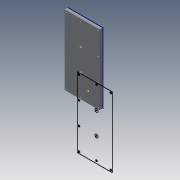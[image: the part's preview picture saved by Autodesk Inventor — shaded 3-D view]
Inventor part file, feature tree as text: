
AUTODESK INVENTOR PART (.ipt)
format: ipt  version: 2015 (Build 190159000, 159)  size: 136,192 bytes
history: native  units: mm
features: other x5, sketch x2, extrude x1, projected_geometry x1
ambient origin geometry x8: Origin, YZ Plane, XZ Plane, XY Plane, X Axis, Y Axis, Z Axis, Center Point
bodies: Body1 (feature_tree)
feature tree (9):
  other  "Blocks"
  extrude  "Extrusion5"  Depth=10.0mm
  sketch  "Sketch2"  dims[d9=70.0mm d13=35.0mm d14=50.0mm d17=75.0mm d18=185.0mm d19=35.0mm d22=5.0mm d23=5.0mm d24=5.0mm d25=5.0mm d26=5.0mm d27=5.0mm d28=5.0mm d29=5.0mm d30=5.0mm d31=5.0mm d32=5.0mm d33=75.0mm d34=5.0mm d35=75.0mm d36=5.0mm d37=5.0mm d38=5.0mm d39=5.0mm d42=5.0mm d43=50.0mm d46=5.0mm d47=5.0mm d48=50.0mm d49=10.0mm d50=0.0mm]
  other  "DXF"
  sketch  "Sketch1"  dims[d2=200.0mm d5=10.0mm]
  projected_geometry  "Projected Loop1"
  other  "Block1"
  other  "Block1:1"
  other  "Block1:2"
